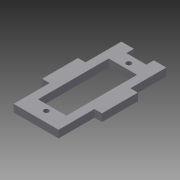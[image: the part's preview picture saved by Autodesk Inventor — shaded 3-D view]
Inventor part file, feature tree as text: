
AUTODESK INVENTOR PART (.ipt)
format: ipt  version: 2013 (Build 170138000, 138)  size: 116,224 bytes
history: native  units: in
note: dims shown in document units (in); Inventor stores cm internally (conversion verified against a paired STEP export)
features: extrude x3, sketch x3
ambient origin geometry x8: Origin, YZ Plane, XZ Plane, XY Plane, X Axis, Y Axis, Z Axis, Center Point
bodies: Solid1 (feature_tree)
feature tree (6):
  extrude  "Extrusion1"  Depth=1.8in
  sketch  "Sketch2"  dims[d2=0.125in d3=0.6in]
  extrude  "Extrusion2"  Depth=0.6in
  extrude  "Extrusion3"  Depth=0.6in
  sketch  "Sketch1"  dims[d0=0.75in d1=1.8in]
  sketch  "Sketch3"  dims[d4=0.125in d5=0.6in d6=0.6in d7=0.125in d8=0.0in d9=0.3333in d10=0.125in d11=0.3333in d12=0.125in d13=0.0in d14=0.4724in d15=1.1811in d16=0.2638in d17=0.35in d18=0.083in d19=0.0984in d20=0.083in d21=0.0984in d22=0.2362in d23=0.2362in d24=0.125in d25=0.0in]
